# Revit family: EV- Series
name_source: partatom
category: Lighting Fixtures
units: mm (PartAtom-declared; Revit-internal decimal feet)

## family parameters
Cut with Voids When Loaded = No
Host = Face
Light Source = No
OmniClass Number = 23.80.70.11
OmniClass Title = Luminaries for Internal Lighting
Part Type = Normal
Room Calculation Point = No
Round Connector Dimension = Use Diameter
Shared = Yes

## types (2) — shared parameters
Apparent Load = 0 VA
Default Elevation = 48.00"
Description = The EV Series is a compact architectural emergency lighting unit designed for fast wall mount installation and reliable service
Finish = White
Lens = White Glass
Manufacturer = Dual Lighting
Model = EV
URL = https://www.currentlighting.com
Voltage = 120 V

## per-type parameters (varying)
| type | Photometric Web | Total Input Wattage |
| EV4-02L | Web - EV : EV-02L | 4 - Watts |
| EV2 | Web - EV : EV | 2 - Watts |

## geometry (parser evidence)
native form markers: Blend x4, Sweep x4
no freeform markers — native parametric forms only
